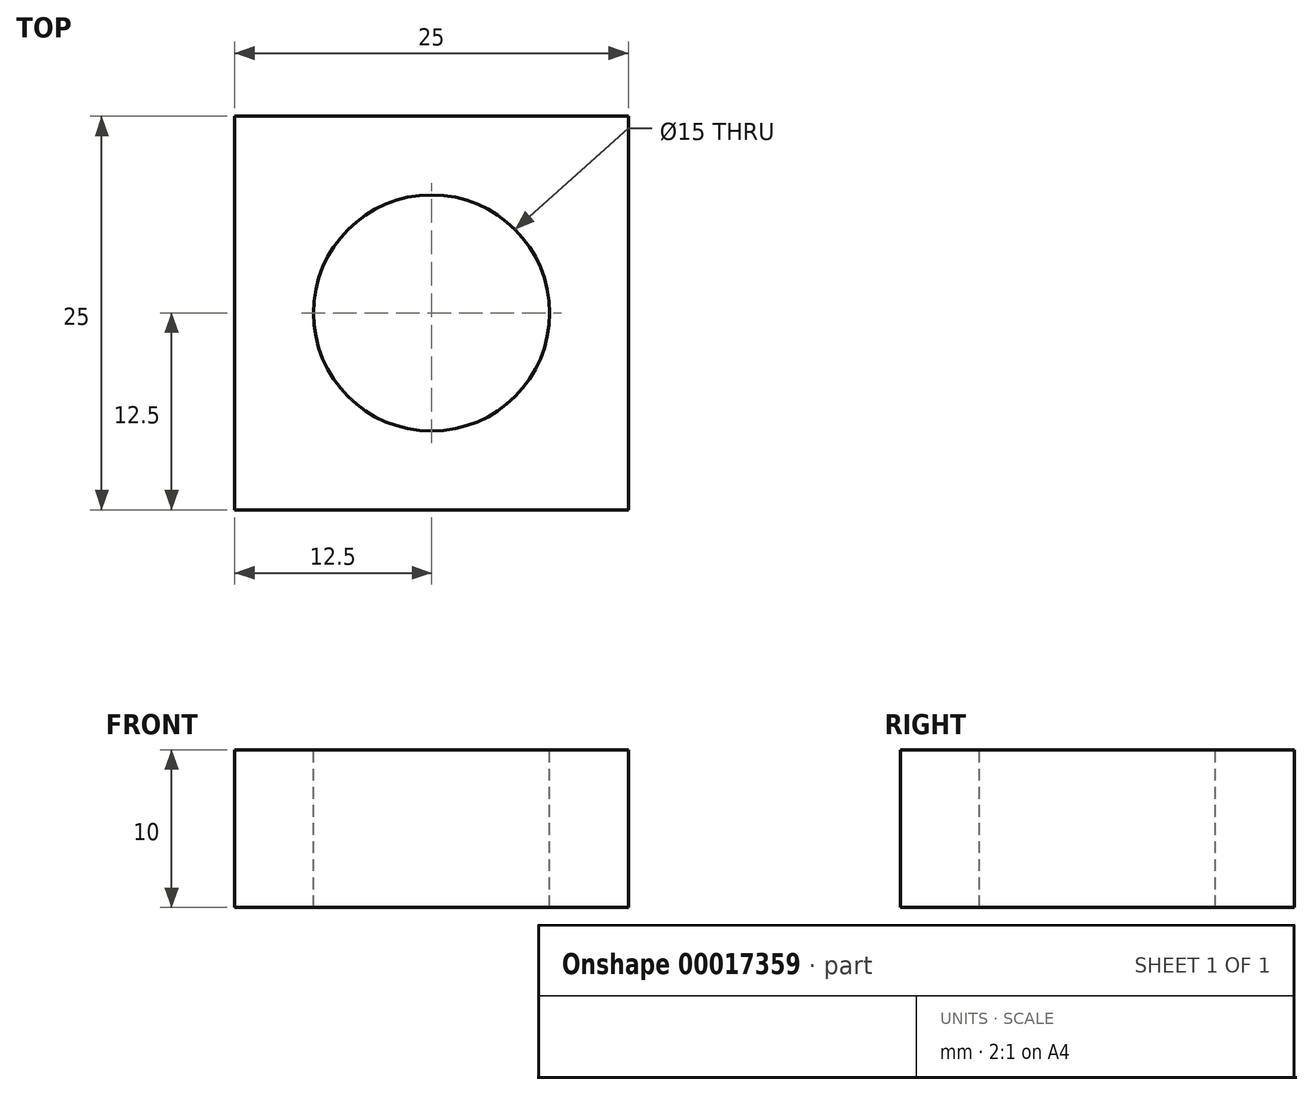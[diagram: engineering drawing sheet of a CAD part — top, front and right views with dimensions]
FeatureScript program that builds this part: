
annotation { "Feature Type Name" : "Feature", "Feature Type Description" : "" }
export const myFeature = defineFeature(function(context is Context, id is Id, definition is map)
    precondition{}
    {
        {
            var Q0;
            Q0=qCreatedBy(makeId("Front.planeOp"),FACE);
            var sketch = newSketch(context, id + "F0", { "sketchPlane" : qUnion([Q0])});
            skLineSegment(sketch, "E0.bottom", {"start": v(-8.98, -2.54) * mm, "end": v(16.02, -2.54) * mm});
            skLineSegment(sketch, "E0.top", {"start": v(-8.98, -12.54) * mm, "end": v(16.02, -12.54) * mm});
            skLineSegment(sketch, "E0.left", {"start": v(-8.98, -2.54) * mm, "end": v(-8.98, -12.54) * mm});
            skLineSegment(sketch, "E0.right", {"start": v(16.02, -2.54) * mm, "end": v(16.02, -12.54) * mm});
            skSolve(sketch);
        }
        {
            var Q0;
            Q0=makeQuery(id+"F0.imprint","IMPRINT",FACE,{"disambiguationData":[TD([[makeQuery(id+"F0.imprint","IMPRINT",EDGE,{"derivedFrom":sQuery(id+"F0.wireOp",EDGE,"E0.bottom")}),-1.0]])]});
            extrude(context, id + "F1", {"entities" : qUnion([Q0]), "depth" : 25 * mm});
        }
        {
            var Q0;
            Q0=makeQuery(id+"F1.opExtrude","SWEPT_FACE",FACE,{"disambiguationData":[OSD([sQuery(id+"F0.wireOp",EDGE,"E0.bottom")])]});
            var sketch = newSketch(context, id + "F2", { "sketchPlane" : qUnion([Q0])});
            skCircle(sketch, "E1", {"center": v(3.52, -12.5) * mm, "radius": 7.5 * mm});
            skSolve(sketch);
        }
        {
            var Q0;
            Q0=makeQuery(id+"F2.imprint","IMPRINT",FACE,{"disambiguationData":[TD([[makeQuery(id+"F2.imprint","IMPRINT",EDGE,{"derivedFrom":sQuery(id+"F2.wireOp",EDGE,"E1")}),1.0]])]});
            extrude(context, id + "F3", {"entities" : qUnion([Q0]), "operationType" : NewBodyOperationType.REMOVE, "oppositeDirection" : true, "depth" : 25 * mm});
        }
    });
